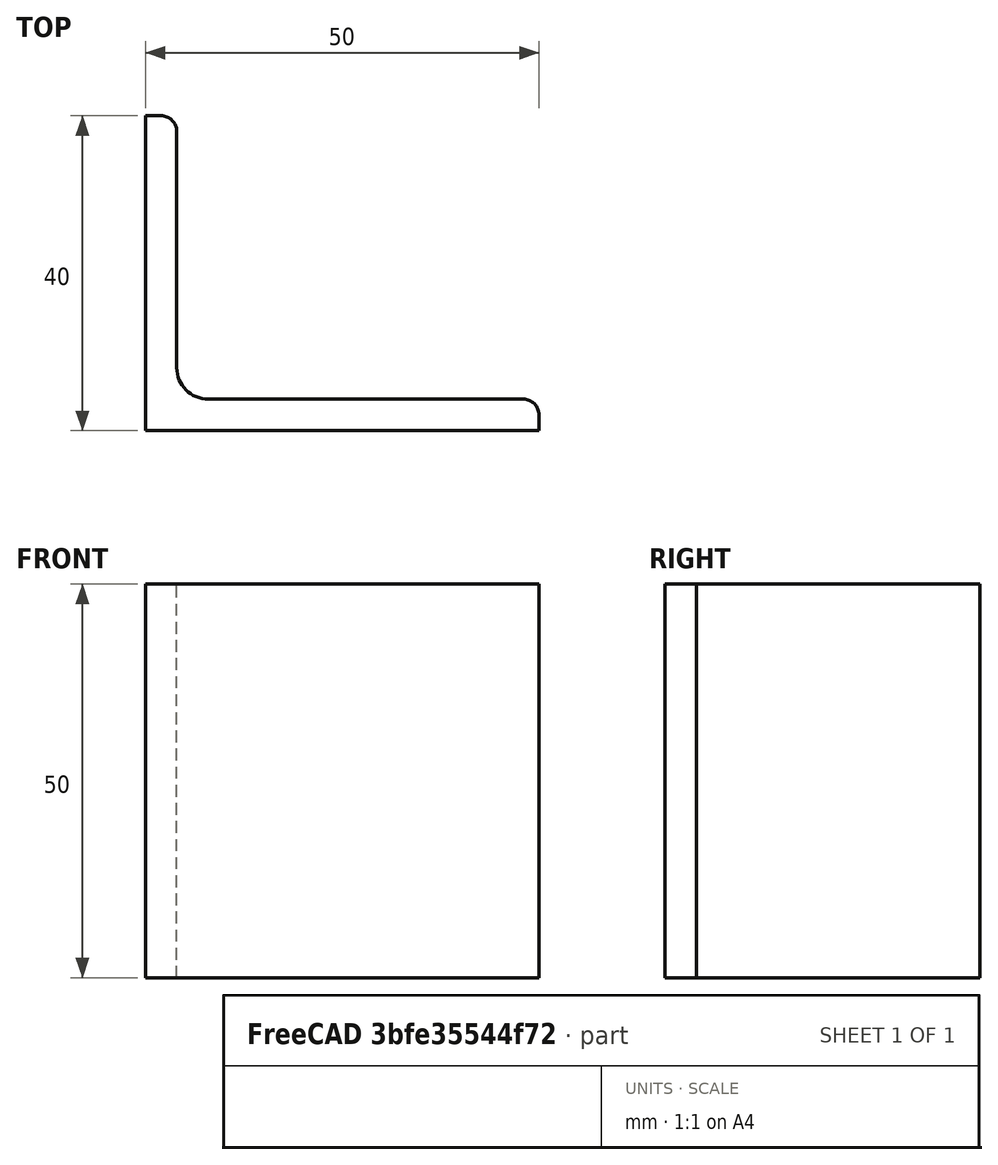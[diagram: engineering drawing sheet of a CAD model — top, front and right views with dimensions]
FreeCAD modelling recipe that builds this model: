
FCSTD DOCUMENT  (FreeCAD 0.15R4671 (Git))
Label: Angle Bar 50x40x4 EN10056 S235JR
License: All rights reserved
LicenseURL: http://en.wikipedia.org/wiki/All_rights_reserved
objects: Sketcher::SketchObject×1, Part::Extrusion×1
note: 2 computed .brp shape members not serialized (recipe doc carries the construction recipe); baked Part::Feature solids carry a one-line shape summary decoded from their .brp

FEATURE [Sketcher::SketchObject] Sketch
  sketch-geometry (9):
    g0: LineSegment StartX=0 StartY=0 StartZ=0 EndX=50 EndY=0 EndZ=0
    g1: LineSegment StartX=50 StartY=0 StartZ=0 EndX=50 EndY=2 EndZ=0
    g2: LineSegment StartX=48 StartY=4 StartZ=0 EndX=8 EndY=4 EndZ=0
    g3: LineSegment StartX=0 StartY=0 StartZ=0 EndX=0 EndY=40 EndZ=0
    g4: LineSegment StartX=0 StartY=40 StartZ=0 EndX=2 EndY=40 EndZ=0
    g5: LineSegment StartX=4 StartY=38 StartZ=0 EndX=4 EndY=8 EndZ=0
    g6: ArcOfCircle CenterX=8 CenterY=8 CenterZ=0 NormalX=0 NormalY=0 NormalZ=1 Radius=4 StartAngle=3.14159 EndAngle=4.71239
    g7: ArcOfCircle CenterX=2 CenterY=38 CenterZ=0 NormalX=0 NormalY=0 NormalZ=1 Radius=2 StartAngle=0 EndAngle=1.5708
    g8: ArcOfCircle CenterX=48 CenterY=2 CenterZ=0 NormalX=0 NormalY=0 NormalZ=1 Radius=2 StartAngle=0 EndAngle=1.5708
  constraints (23):
    c: Coincident(g0,g-1)
    c: Horizontal(g0)
    c: Coincident(g1,g0)
    c: Vertical(g1)
    c: Horizontal(g2)
    c: Coincident(g3,g-1)
    c: Vertical(g3)
    c: Coincident(g4,g3)
    c: Horizontal(g4)
    c: Vertical(g5)
    c: Tangent(g5,g6) = -1.5708
    c: Tangent(g2,g6) = 1.5708
    c: Tangent(g4,g7) = 1.5708
    c: Tangent(g5,g7) = 1.5708
    c: Tangent(g2,g8) = -1.5708
    c: Tangent(g1,g8) = -1.5708
    c: DistanceX(g0) = 50
    c: DistanceY(g3) = 40
    c: DistanceY(g0,g2) = 4
    c: DistanceX(g3,g5) = 4
    c: Radius(g6) = 4
    c: Radius(g8) = 2
    c: Radius(g7) = 2
FEATURE [Part::Extrusion] Extrude  label="Angle Bar 50x40x4 EN10056 S235JR"
  Base = -> Sketch
  Dir = (0,0,50)
  Solid = true
